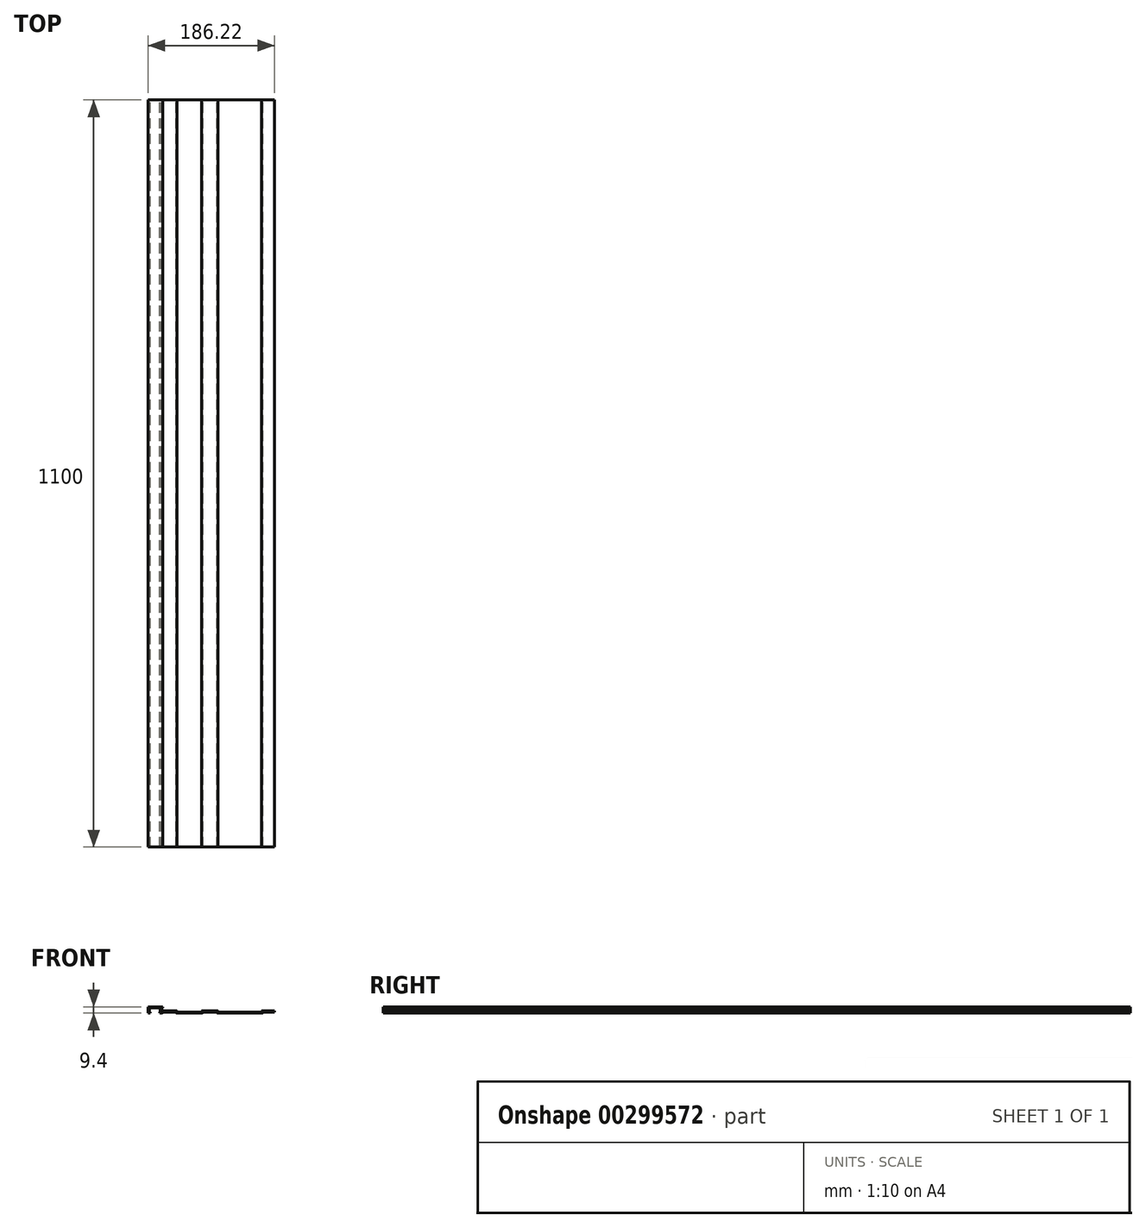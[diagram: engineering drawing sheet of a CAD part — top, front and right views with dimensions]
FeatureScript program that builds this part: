
annotation { "Feature Type Name" : "Feature", "Feature Type Description" : "" }
export const myFeature = defineFeature(function(context is Context, id is Id, definition is map)
    precondition{}
    {
        {
            var Q0;
            Q0=qCreatedBy(makeId("Front.planeOp"),FACE);
            var sketch = newSketch(context, id + "F0", { "sketchPlane" : qUnion([Q0])});
            skLineSegment(sketch, "E0", {"start": v(0, 0) * mm, "end": v(21.92, 0) * mm});
            skLineSegment(sketch, "E1", {"start": v(21.92, 0) * mm, "end": v(21.92, -1.7) * mm});
            skLineSegment(sketch, "E2", {"start": v(21.92, -1.7) * mm, "end": v(20.17, -1.7) * mm});
            skLineSegment(sketch, "E3", {"start": v(20.17, -1.7) * mm, "end": v(20.17, -6) * mm});
            skLineSegment(sketch, "E4", {"start": v(20.17, -6) * mm, "end": v(42.07, -6) * mm});
            skLineSegment(sketch, "E5", {"start": v(43.77, -7.7) * mm, "end": v(77.87, -7.7) * mm});
            skLineSegment(sketch, "E6", {"start": v(79.57, -6) * mm, "end": v(102.37, -6) * mm});
            skLineSegment(sketch, "E7", {"start": v(104.07, -7.7) * mm, "end": v(166.37, -7.7) * mm});
            skLineSegment(sketch, "E8", {"start": v(168.07, -6) * mm, "end": v(186.22, -6) * mm});
            skLineSegment(sketch, "E9", {"start": v(0, 0) * mm, "end": v(0, -9.4) * mm});
            skLineSegment(sketch, "E10", {"start": v(0, -9.4) * mm, "end": v(3.5, -9.4) * mm});
            skLineSegment(sketch, "E11", {"start": v(186.22, -6) * mm, "end": v(186.22, -7.7) * mm});
            skLineSegment(sketch, "E12", {"start": v(100.67, -7.7) * mm, "end": v(81.27, -7.7) * mm});
            skLineSegment(sketch, "E13", {"start": v(79.57, -9.4) * mm, "end": v(42.07, -9.4) * mm});
            skLineSegment(sketch, "E14", {"start": v(40.37, -7.7) * mm, "end": v(22.25, -7.7) * mm});
            skLineSegment(sketch, "E15", {"start": v(18, -1.7) * mm, "end": v(1.7, -1.7) * mm});
            skLineSegment(sketch, "E16", {"start": v(1.7, -1.7) * mm, "end": v(1.7, -7.7) * mm});
            skLineSegment(sketch, "E17", {"start": v(1.7, -7.7) * mm, "end": v(3.5, -7.7) * mm});
            skLineSegment(sketch, "E18", {"start": v(3.5, -7.7) * mm, "end": v(3.5, -9.4) * mm});
            skPoint(sketch, "E19.visualSharp", {"position": v(167.22, -6) * mm});
            skLineSegment(sketch, "E20", {"start": v(186.22, -7.7) * mm, "end": v(169.77, -7.7) * mm});
            skLineSegment(sketch, "E21", {"start": v(168.07, -9.4) * mm, "end": v(102.37, -9.4) * mm});
            skPoint(sketch, "E22.visualSharp", {"position": v(103.22, -6) * mm});
            skPoint(sketch, "E23.visualSharp", {"position": v(42.92, -6) * mm});
            skLineSegment(sketch, "E24", {"start": v(18, -1.7) * mm, "end": v(18, -7.7) * mm});
            skLineSegment(sketch, "E25", {"start": v(18, -7.7) * mm, "end": v(17.05, -7.7) * mm});
            skLineSegment(sketch, "E26", {"start": v(17.05, -7.7) * mm, "end": v(17.05, -9.4) * mm});
            skLineSegment(sketch, "E27", {"start": v(17.05, -9.4) * mm, "end": v(20.55, -9.4) * mm});
            skPoint(sketch, "E28", {"position": v(22.25, -7.7) * mm});
            skPoint(sketch, "E29.visualSharp", {"position": v(20.55, -9.4) * mm});
            skLineSegment(sketch, "E30", {"start": v(21.4, -8.55) * mm, "end": v(21.4, -8.55) * mm});
            skLineSegment(sketch, "E31", {"start": v(42.92, -6.85) * mm, "end": v(42.92, -6.85) * mm});
            skLineSegment(sketch, "E32", {"start": v(41.22, -8.55) * mm, "end": v(41.22, -8.55) * mm});
            skArc(sketch, "E33.filletArc", {"start": v(41.22, -8.55) * mm, "mid": v(40.97, -7.95) * mm, "end": v(40.37, -7.7) * mm});
            skArc(sketch, "E34.filletArc", {"start": v(41.22, -8.55) * mm, "mid": v(41.47, -9.15) * mm, "end": v(42.07, -9.4) * mm});
            skArc(sketch, "E35.filletArc", {"start": v(42.92, -6.85) * mm, "mid": v(42.67, -6.25) * mm, "end": v(42.07, -6) * mm});
            skPoint(sketch, "E36.visualSharp", {"position": v(42.92, -7.7) * mm});
            skArc(sketch, "E36.filletArc", {"start": v(42.92, -6.85) * mm, "mid": v(43.17, -7.45) * mm, "end": v(43.77, -7.7) * mm});
            skLineSegment(sketch, "E37", {"start": v(78.72, -6.85) * mm, "end": v(78.72, -6.85) * mm});
            skLineSegment(sketch, "E38.0", {"start": v(80.42, -8.55) * mm, "end": v(80.42, -8.55) * mm});
            skPoint(sketch, "E39.visualSharp", {"position": v(80.42, -9.4) * mm});
            skArc(sketch, "E39.filletArc", {"start": v(79.57, -9.4) * mm, "mid": v(80.17, -9.15) * mm, "end": v(80.42, -8.55) * mm});
            skPoint(sketch, "E40.visualSharp", {"position": v(80.42, -7.7) * mm});
            skArc(sketch, "E40.filletArc", {"start": v(81.27, -7.7) * mm, "mid": v(80.67, -7.95) * mm, "end": v(80.42, -8.55) * mm});
            skPoint(sketch, "E41.visualSharp", {"position": v(78.72, -7.7) * mm});
            skArc(sketch, "E41.filletArc", {"start": v(77.87, -7.7) * mm, "mid": v(78.47, -7.45) * mm, "end": v(78.72, -6.85) * mm});
            skPoint(sketch, "E42.visualSharp", {"position": v(78.72, -6) * mm});
            skArc(sketch, "E42.filletArc", {"start": v(79.57, -6) * mm, "mid": v(78.97, -6.25) * mm, "end": v(78.72, -6.85) * mm});
            skPoint(sketch, "E43.visualSharp", {"position": v(21.4, -7.7) * mm});
            skArc(sketch, "E43.filletArc", {"start": v(22.25, -7.7) * mm, "mid": v(21.65, -7.95) * mm, "end": v(21.4, -8.55) * mm});
            skPoint(sketch, "E44.visualSharp", {"position": v(21.4, -9.4) * mm});
            skArc(sketch, "E44.filletArc", {"start": v(20.55, -9.4) * mm, "mid": v(21.15, -9.15) * mm, "end": v(21.4, -8.55) * mm});
            skLineSegment(sketch, "E45", {"start": v(167.22, -6.85) * mm, "end": v(167.22, -6.85) * mm});
            skLineSegment(sketch, "E46.0", {"start": v(168.92, -8.55) * mm, "end": v(168.92, -8.55) * mm});
            skPoint(sketch, "E47.visualSharp", {"position": v(167.22, -7.7) * mm});
            skArc(sketch, "E47.filletArc", {"start": v(166.37, -7.7) * mm, "mid": v(166.97, -7.45) * mm, "end": v(167.22, -6.85) * mm});
            skArc(sketch, "E48.filletArc", {"start": v(168.07, -6) * mm, "mid": v(167.47, -6.25) * mm, "end": v(167.22, -6.85) * mm});
            skPoint(sketch, "E49.visualSharp", {"position": v(168.92, -7.7) * mm});
            skArc(sketch, "E49.filletArc", {"start": v(169.77, -7.7) * mm, "mid": v(169.17, -7.95) * mm, "end": v(168.92, -8.55) * mm});
            skPoint(sketch, "E50.visualSharp", {"position": v(168.92, -9.4) * mm});
            skArc(sketch, "E50.filletArc", {"start": v(168.07, -9.4) * mm, "mid": v(168.67, -9.15) * mm, "end": v(168.92, -8.55) * mm});
            skLineSegment(sketch, "E51", {"start": v(103.22, -6.85) * mm, "end": v(103.22, -6.85) * mm});
            skLineSegment(sketch, "E52.0", {"start": v(101.52, -8.55) * mm, "end": v(101.52, -8.55) * mm});
            skArc(sketch, "E53.filletArc", {"start": v(103.22, -6.85) * mm, "mid": v(102.97, -6.25) * mm, "end": v(102.37, -6) * mm});
            skPoint(sketch, "E54.visualSharp", {"position": v(103.22, -7.7) * mm});
            skArc(sketch, "E54.filletArc", {"start": v(103.22, -6.85) * mm, "mid": v(103.47, -7.45) * mm, "end": v(104.07, -7.7) * mm});
            skPoint(sketch, "E55.visualSharp", {"position": v(101.52, -7.7) * mm});
            skArc(sketch, "E55.filletArc", {"start": v(101.52, -8.55) * mm, "mid": v(101.27, -7.95) * mm, "end": v(100.67, -7.7) * mm});
            skPoint(sketch, "E56.visualSharp", {"position": v(101.52, -9.4) * mm});
            skArc(sketch, "E56.filletArc", {"start": v(101.52, -8.55) * mm, "mid": v(101.77, -9.15) * mm, "end": v(102.37, -9.4) * mm});
            skSolve(sketch);
        }
        {
            var Q0;
            Q0 = qSketchRegion(id + "F0", true);
            extrude(context, id + "F1", {"entities" : qUnion([Q0]), "depth" : 1100 * mm});
        }
    });
